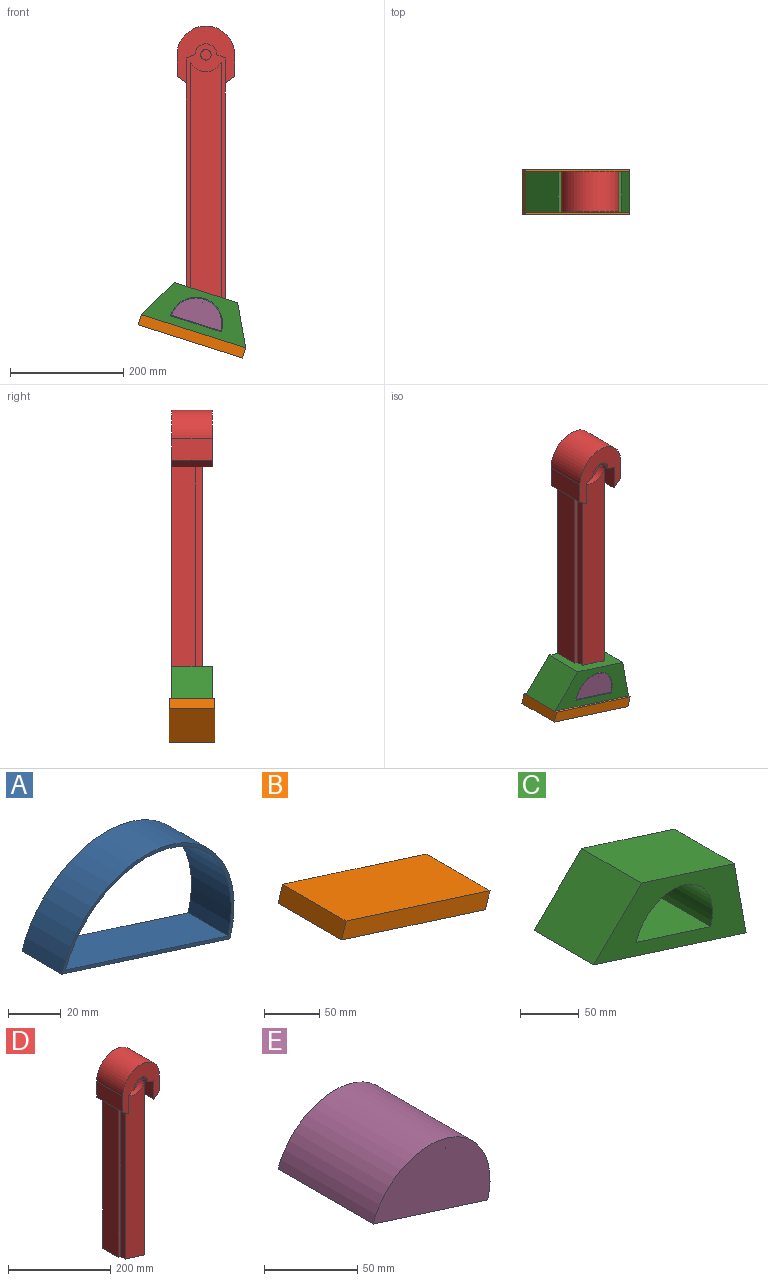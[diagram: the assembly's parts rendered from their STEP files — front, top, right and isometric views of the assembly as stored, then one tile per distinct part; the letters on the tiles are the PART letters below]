
ASSEMBLY  parts=5 mates=4
PART A: 6 faces, bbox 92.2x21.3x61.5 mm
  f0: plane 87.05x27.64mm, normal (0.3,0,0.95), area 1948.7mm2, adj f3,f4,f5
  f1: cylinder r=47.22mm len=92.22mm, axis (0,1,0), area 3164.8mm2, adj f2,f4,f5
  f2: plane 90x28.58mm, normal (-0.3,0,-0.95), area 2014.8mm2, adj f1,f4,f5
  f3: cylinder r=45.69mm len=88.75mm, axis (0,1,0), area 2997.6mm2, adj f0,f4,f5
  f4: plane 92.22x61.51mm, normal (0,-1,0), area 361.6mm2, adj f0,f1,f2,f3
  f5: plane 92.22x61.51mm, normal (0,1,0), area 361.6mm2, adj f0,f1,f2,f3
PART B: 6 faces, bbox 189.4x81x76.4 mm
  f0: plane 183.65x81.03mm, normal (0.3,0,0.95), area 15612.8mm2, adj f1,f3,f4,f5
  f1: plane 81.03x18.08mm, normal (-0.95,0,0.3), area 1537mm2, adj f0,f2,f4,f5
  f2: plane 183.65x81.03mm, normal (-0.3,0,-0.95), area 15612.8mm2, adj f1,f3,f4,f5
  f3: plane 81.03x18.08mm, normal (0.95,0,-0.3), area 1537mm2, adj f0,f2,f4,f5
  f4: plane 189.39x76.4mm, normal (0,-1,0), area 3655.2mm2, adj f0,f1,f2,f3
  f5: plane 189.39x76.4mm, normal (0,1,0), area 3655.2mm2, adj f0,f1,f2,f3
PART C: 8 faces, bbox 183.7x72.1x115 mm
  f0: plane 72.14x57.54mm, normal (-0.7,0,0.71), area 5828mm2, adj f1,f5,f6,f7
  f1: plane 183.65x72.14mm, normal (-0.3,0,-0.95), area 13899.8mm2, adj f0,f2,f6,f7
  f2: plane 79.52x72.14mm, normal (0.98,0,0.18), area 5828mm2, adj f1,f5,f6,f7
  f3: plane 90x72.14mm, normal (0.3,0,0.95), area 6811.8mm2, adj f4,f6,f7
  f4: cylinder r=47.22mm len=92.22mm, axis (0,1,0), area 10700mm2, adj f3,f6,f7
  f5: plane 111.83x72.14mm, normal (0.3,0,0.95), area 8463.7mm2, adj f0,f2,f6,f7
  f6: plane 183.65x115.03mm, normal (0,-1,0), area 7576.2mm2, adj f0,f1,f2,f3,f4,f5
  f7: plane 183.65x115.03mm, normal (0,1,0), area 7576.2mm2, adj f0,f1,f2,f3,f4,f5
PART D: 22 faces, bbox 101.6x72.1x481.5 mm
  f0: plane 44.06x29.21mm, normal (1,0,0), area 1286.9mm2, adj f1,f2,f10,f16
  f1: plane 72.14x16.28mm, normal (-0.58,0,-0.81), area 1442.9mm2, adj f0,f9,f10,f11,f13
  f2: plane 29.21x15.26mm, normal (0.35,0,-0.94), area 475.6mm2, adj f0,f3,f10,f16
  f3: cylinder r=19.26mm len=38.52mm, axis (0,1,0), area 1767.3mm2, adj f2,f4,f10,f16
  f4: plane 29.21x15.26mm, normal (-0.35,0,-0.94), area 475.6mm2, adj f3,f5,f10,f16
  f5: plane 44.06x29.21mm, normal (-1,0,0), area 1286.9mm2, adj f4,f6,f10,f16
  f6: plane 72.14x16.28mm, normal (0.58,0,-0.81), area 1442.9mm2, adj f5,f7,f10,f11,f12
  f7: plane 72.14x38.1mm, normal (1,0,0), area 2748.4mm2, adj f6,f8,f10,f11
  f8: cylinder r=50.8mm len=101.6mm, axis (0,1,0), area 11512.4mm2, adj f7,f9,f10,f11
  f9: plane 72.14x38.1mm, normal (-1,0,0), area 2748.4mm2, adj f1,f8,f10,f11
  f10: plane 101.6x100.53mm, normal (0,-1,0), area 4987.2mm2, adj f0,f1,f2,f3,f4,f5,f6,f7
  f11: plane 481.53x101.6mm, normal (0,1,0), area 34465.8mm2, adj f1,f6,f7,f8,f9,f12,f13,f14
  f12: plane 381x42.93mm, normal (1,0,0), area 16354.8mm2, adj f6,f11,f14,f16
  f13: plane 359.07x42.93mm, normal (-1,0,0), area 15413.6mm2, adj f1,f11,f14,f16
  f14: plane 69.05x54.86mm, normal (-0.3,0,-0.95), area 3783.3mm2, adj f11,f12,f13,f16,f17,f18,f20
  f15: cylinder r=9.27mm len=21.59mm, axis (0,1,0), area 1258.2mm2, adj f16,f21
  f16: plane 449.98x69.05mm, normal (0,-1,0), area 7979.6mm2, adj f0,f2,f3,f4,f5,f12,f13,f14
  f17: plane 398.32x11.94mm, normal (-1,0,0), area 4755.1mm2, adj f14,f16,f19,f20
  f18: plane 415.4x11.94mm, normal (1,0,0), area 4959mm2, adj f14,f16,f19,f20
  f19: cylinder r=29.83mm len=53.78mm, axis (0,1,0), area 800mm2, adj f16,f17,f18,f20
  f20: plane 415.4x53.78mm, normal (0,-1,0), area 21228.8mm2, adj f14,f17,f18,f19
  f21: plane 18.55x18.55mm, normal (0,-1,0), area 270.2mm2, adj f15
PART E: 7 faces, bbox 88.8x72.1x58.1 mm
  f0: plane 87.05x72.14mm, normal (-0.3,0,-0.95), area 6588.3mm2, adj f4,f5,f6
  f1: plane 72.14x0.44mm, normal (0.95,0,-0.3), area 33.1mm2, adj f2,f3,f5,f6
  f2: plane 72.14x0.44mm, normal (-1,0,0), area 31.5mm2, adj f1,f3,f5,f6
  f3: plane 72.14x0.14mm, normal (0,0,1), area 10mm2, adj f1,f2,f5,f6
  f4: cylinder r=45.69mm len=88.75mm, axis (0,1,0), area 10134.7mm2, adj f0,f5,f6
  f5: plane 88.75x58.06mm, normal (0,-1,0), area 3140.1mm2, adj f0,f1,f2,f3,f4
  f6: plane 88.75x58.06mm, normal (0,1,0), area 3140.1mm2, adj f0,f1,f2,f3,f4
PLACE A t=(-59.29,211.78,37.62)mm
PLACE B t=(-59.29,216.23,37.62)mm
PLACE C t=(-59.29,211.78,37.62)mm
PLACE D t=(-80.68,211.78,44.41)mm
PLACE E t=(-59.29,211.78,37.62)mm
MATE fastened C.f1 <-> B.f0  axis (-0.3,0,-0.95) through (-51.51,175.72,-405.37)mm
MATE fastened C.f5 <-> D.f14  axis (0.3,0,0.95) through (-29.88,211.78,-337.25)mm
MATE fastened C.f3 <-> A.f2  axis (0.3,0,0.95) through (-47.38,211.78,-392.37)mm
MATE fastened A.f0 <-> E.f0  axis (0.3,0,0.95) through (-46.92,211.78,-390.92)mm
